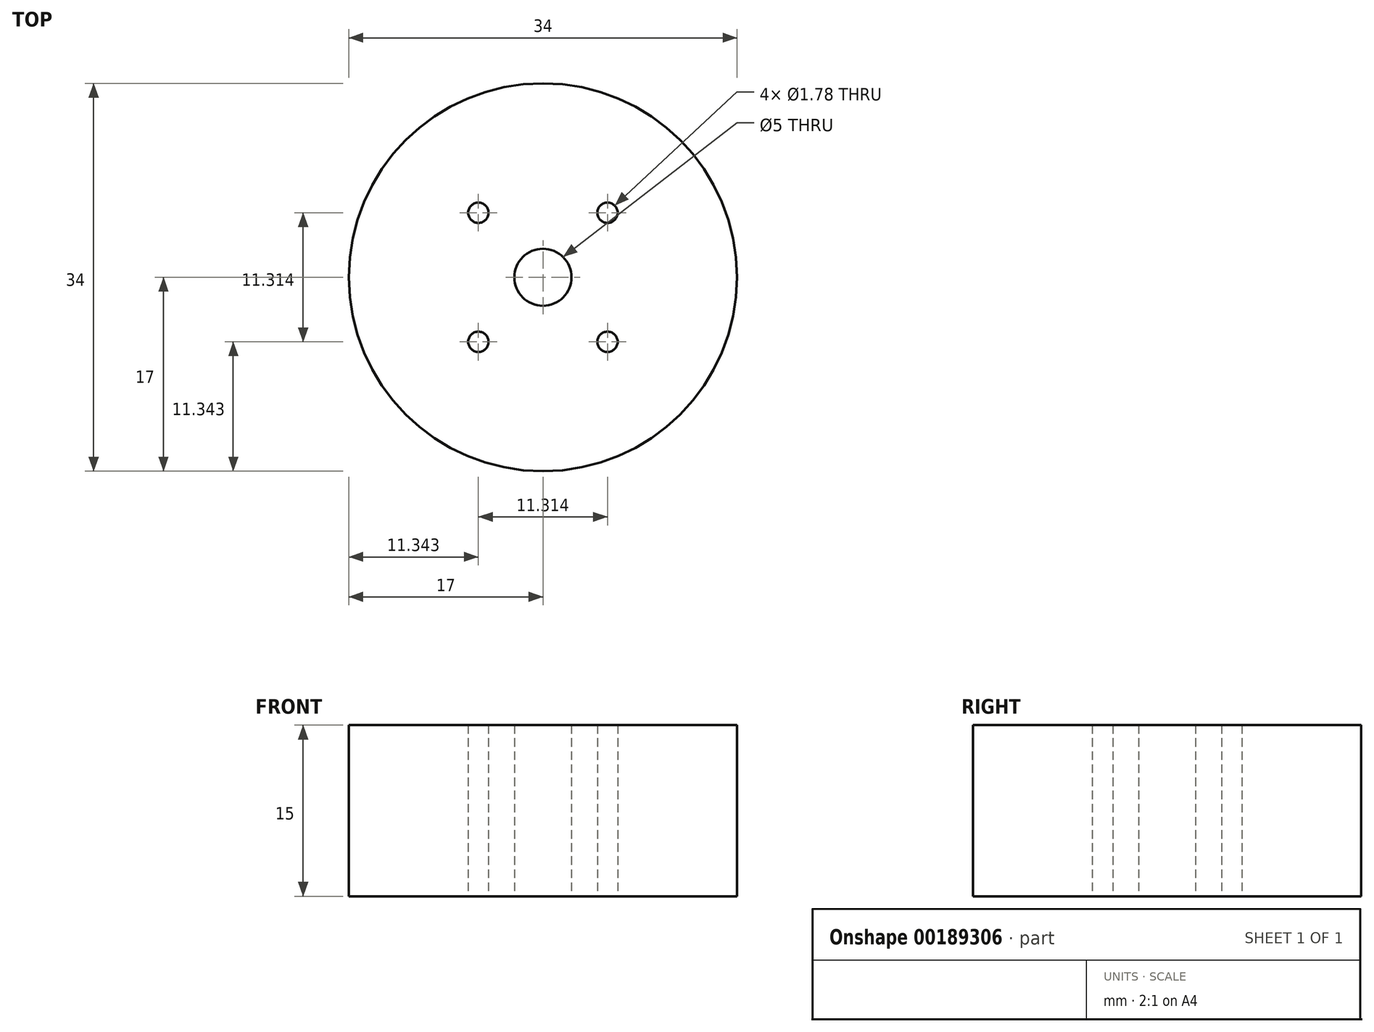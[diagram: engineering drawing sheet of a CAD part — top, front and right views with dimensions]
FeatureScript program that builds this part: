
annotation { "Feature Type Name" : "Feature", "Feature Type Description" : "" }
export const myFeature = defineFeature(function(context is Context, id is Id, definition is map)
    precondition{}
    {
        {
            var Q0;
            Q0=qCreatedBy(makeId("Top.planeOp"),FACE);
            var sketch = newSketch(context, id + "F0", { "sketchPlane" : qUnion([Q0])});
            skCircle(sketch, "E0", {"center": v(0, 0) * mm, "radius": 17 * mm});
            skCircle(sketch, "E1", {"center": v(0, 0) * mm, "radius": 2.5 * mm});
            skCircle(sketch, "E2", {"center": v(-5.66, 5.66) * mm, "radius": 0.89 * mm});
            skLineSegment(sketch, "E3", {"start": v(-5.66, 5.66) * mm, "end": v(0, 0) * mm, "construction": true});
            skCircle(sketch, "E4.MirrorC", {"center": v(5.66, 5.66) * mm, "radius": 0.89 * mm});
            skCircle(sketch, "E5.MirrorC", {"center": v(5.66, -5.66) * mm, "radius": 0.89 * mm});
            skCircle(sketch, "E6.MirrorC", {"center": v(-5.66, -5.66) * mm, "radius": 0.89 * mm});
            skSolve(sketch);
        }
        {
            var Q0;
            Q0=makeQuery(id+"F0.imprint","IMPRINT",FACE,{"disambiguationData":[TD([[makeQuery(id+"F0.imprint","IMPRINT",EDGE,{"derivedFrom":sQuery(id+"F0.wireOp",EDGE,"E0")}),1.0]])]});
            extrude(context, id + "F1", {"entities" : qUnion([Q0]), "depth" : 15 * mm});
        }
    });
